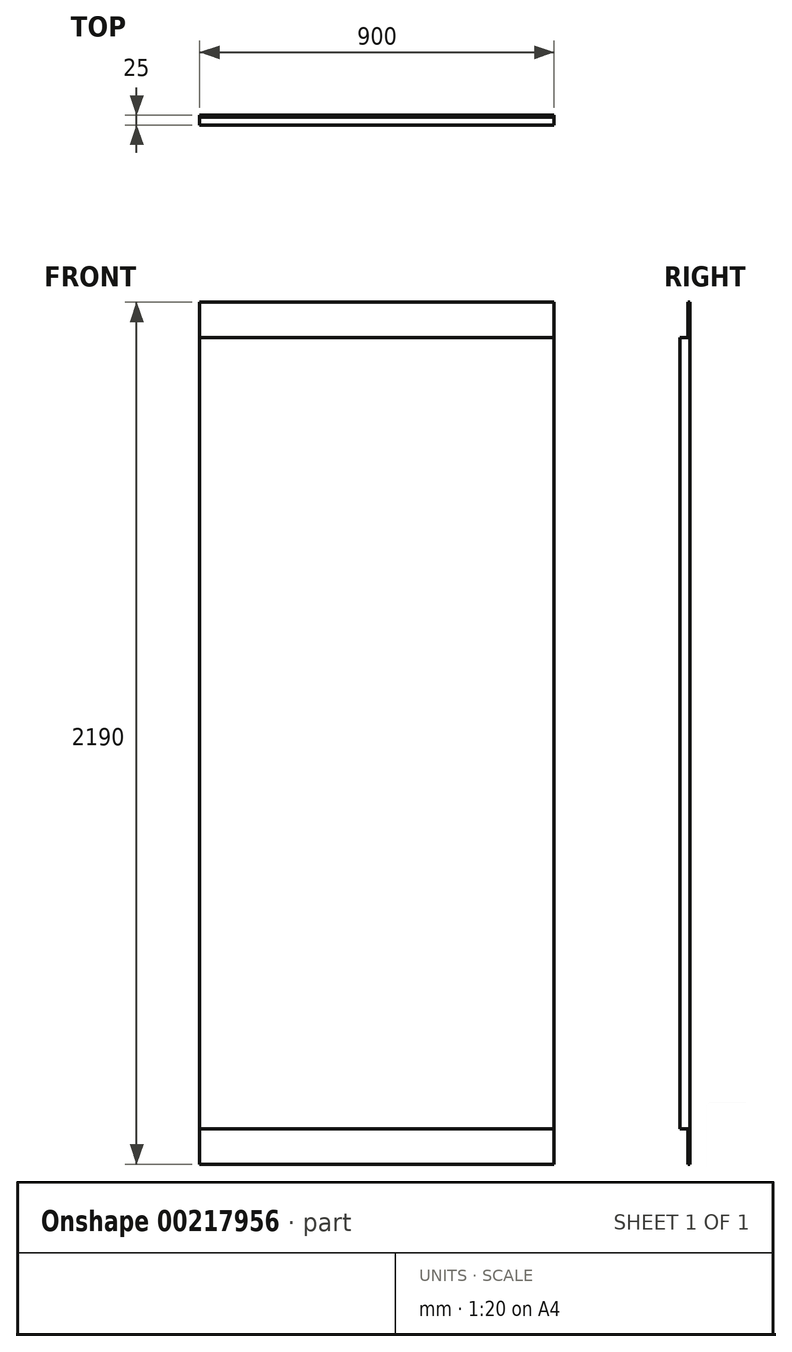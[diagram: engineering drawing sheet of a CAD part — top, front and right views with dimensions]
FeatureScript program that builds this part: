
annotation { "Feature Type Name" : "Feature", "Feature Type Description" : "" }
export const myFeature = defineFeature(function(context is Context, id is Id, definition is map)
    precondition{}
    {
        {
            var Q0;
            Q0=qCreatedBy(makeId("Front.planeOp"),FACE);
            var sketch = newSketch(context, id + "F0", { "sketchPlane" : qUnion([Q0])});
            skLineSegment(sketch, "E0.bottom", {"start": v(0, 0) * mm, "end": v(900, 0) * mm});
            skLineSegment(sketch, "E0.top", {"start": v(0, -2010) * mm, "end": v(900, -2010) * mm});
            skLineSegment(sketch, "E0.left", {"start": v(0, 0) * mm, "end": v(0, -2010) * mm});
            skLineSegment(sketch, "E0.right", {"start": v(900, 0) * mm, "end": v(900, -2010) * mm});
            skLineSegment(sketch, "E1.bottom", {"start": v(0, 0) * mm, "end": v(900, 0) * mm, "construction": true});
            skLineSegment(sketch, "E1.top", {"start": v(0, 90) * mm, "end": v(900, 90) * mm});
            skLineSegment(sketch, "E1.left", {"start": v(0, 0) * mm, "end": v(0, 90) * mm});
            skLineSegment(sketch, "E1.right", {"start": v(900, 0) * mm, "end": v(900, 90) * mm});
            skLineSegment(sketch, "E2.bottom", {"start": v(0, -2010) * mm, "end": v(900, -2010) * mm, "construction": true});
            skLineSegment(sketch, "E2.top", {"start": v(0, -2100) * mm, "end": v(900, -2100) * mm});
            skLineSegment(sketch, "E2.left", {"start": v(0, -2010) * mm, "end": v(0, -2100) * mm});
            skLineSegment(sketch, "E2.right", {"start": v(900, -2010) * mm, "end": v(900, -2100) * mm});
            skSolve(sketch);
        }
        {
            var Q0;
            Q0=makeQuery(id+"F0.imprint","IMPRINT",FACE,{"disambiguationData":[TD([[makeQuery(id+"F0.imprint","IMPRINT",EDGE,{"derivedFrom":sQuery(id+"F0.wireOp",EDGE,"E0.bottom")}),-1.0]])]});
            extrude(context, id + "F1", {"entities" : qUnion([Q0]), "depth" : 25 * mm});
        }
        {
            var Q0;
            Q0=makeQuery(id+"F0.imprint","IMPRINT",FACE,{"disambiguationData":[TD([[makeQuery(id+"F0.imprint","IMPRINT",EDGE,{"derivedFrom":sQuery(id+"F0.wireOp",EDGE,"E0.bottom")}),1.0]])]});
            var Q1;
            Q1=makeQuery(id+"F0.imprint","IMPRINT",FACE,{"disambiguationData":[TD([[makeQuery(id+"F0.imprint","IMPRINT",EDGE,{"derivedFrom":sQuery(id+"F0.wireOp",EDGE,"E0.top")}),-1.0]])]});
            extrude(context, id + "F2", {"entities" : qUnion([Q0, Q1]), "operationType" : NewBodyOperationType.ADD, "depth" : 5 * mm});
        }
    });
